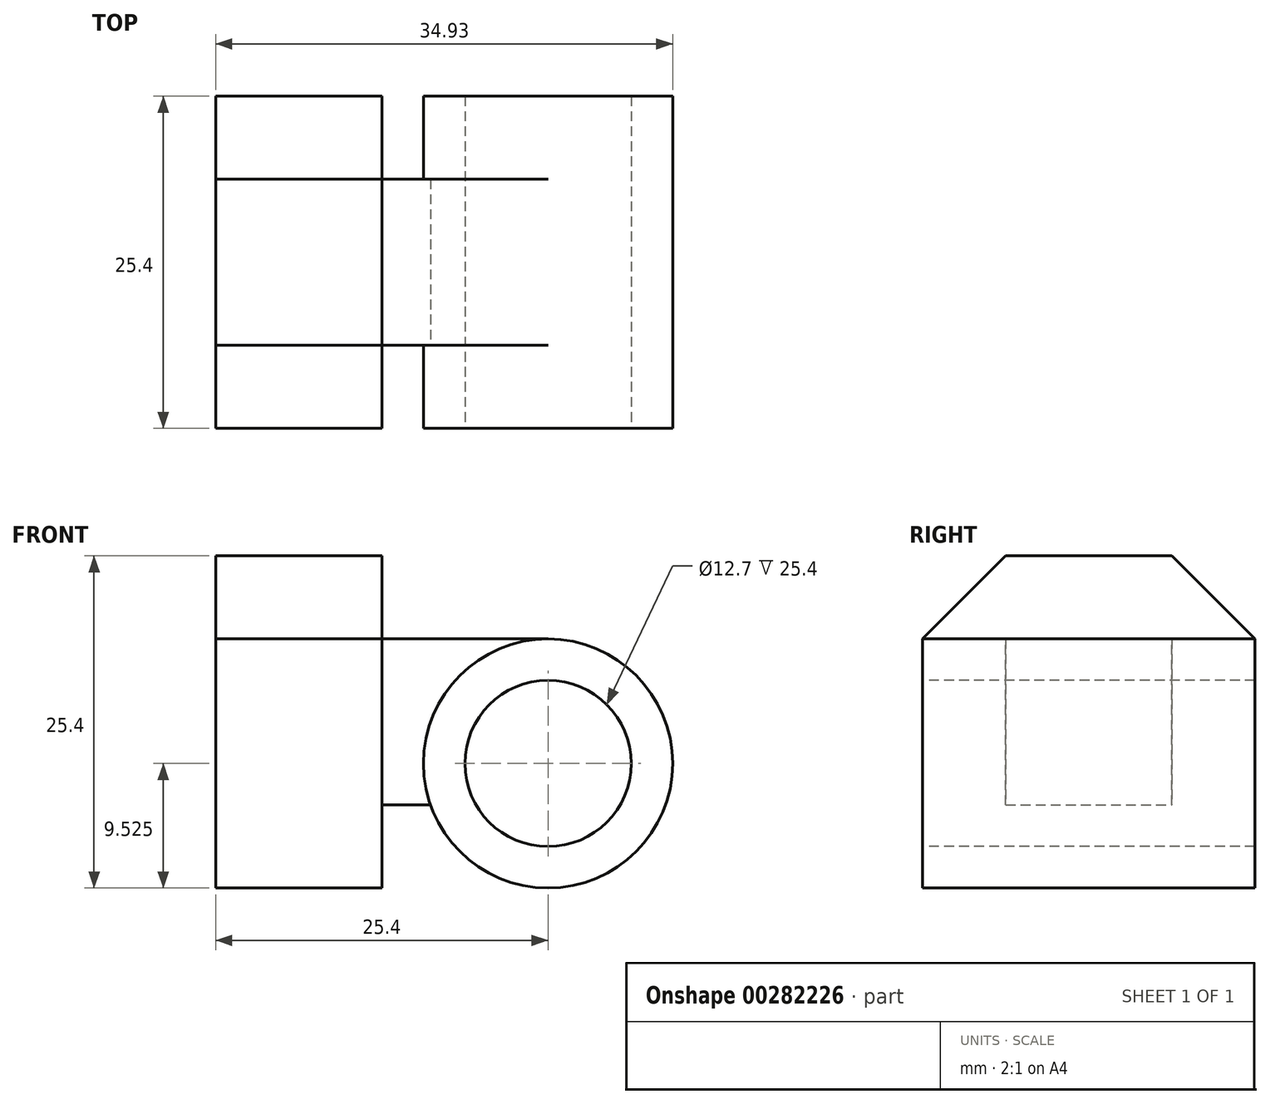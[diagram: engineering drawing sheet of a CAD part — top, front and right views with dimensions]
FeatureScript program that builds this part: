
annotation { "Feature Type Name" : "Feature", "Feature Type Description" : "" }
export const myFeature = defineFeature(function(context is Context, id is Id, definition is map)
    precondition{}
    {
        {
            var Q0;
            Q0=qCreatedBy(makeId("Front.planeOp"),FACE);
            var sketch = newSketch(context, id + "F0", { "sketchPlane" : qUnion([Q0])});
            skLineSegment(sketch, "E0.bottom", {"start": v(0, 0) * mm, "end": v(12.7, 0) * mm});
            skLineSegment(sketch, "E0.top", {"start": v(0, 25.4) * mm, "end": v(12.7, 25.4) * mm});
            skLineSegment(sketch, "E0.left", {"start": v(0, 0) * mm, "end": v(0, 25.4) * mm});
            skLineSegment(sketch, "E0.right", {"start": v(12.7, 0) * mm, "end": v(12.7, 25.4) * mm});
            skSolve(sketch);
        }
        {
            var Q0;
            Q0=makeQuery(id+"F0.imprint","IMPRINT",FACE,{"disambiguationData":[TD([[makeQuery(id+"F0.imprint","IMPRINT",EDGE,{"derivedFrom":sQuery(id+"F0.wireOp",EDGE,"E0.bottom")}),1.0]])]});
            extrude(context, id + "F1", {"entities" : qUnion([Q0]), "endBound" : BoundingType.SYMMETRIC, "depth" : 25.4 * mm});
        }
        {
            var Q0;
            Q0=makeQuery(id+"F1.opExtrude","SWEPT_FACE",FACE,{"disambiguationData":[OSD([sQuery(id+"F0.wireOp",EDGE,"E0.right")])]});
            var sketch = newSketch(context, id + "F2", { "sketchPlane" : qUnion([Q0])});
            skLineSegment(sketch, "E1", {"start": v(-12.7, 19.05) * mm, "end": v(-12.7, 25.4) * mm});
            skLineSegment(sketch, "E2", {"start": v(-12.7, 25.4) * mm, "end": v(-6.35, 25.4) * mm});
            skLineSegment(sketch, "E3", {"start": v(-6.35, 25.4) * mm, "end": v(-12.7, 19.05) * mm});
            skLineSegment(sketch, "E4", {"start": v(6.35, 25.4) * mm, "end": v(12.7, 19.05) * mm});
            skLineSegment(sketch, "E5", {"start": v(12.7, 19.05) * mm, "end": v(12.7, 25.4) * mm});
            skLineSegment(sketch, "E6", {"start": v(12.7, 25.4) * mm, "end": v(6.35, 25.4) * mm});
            skSolve(sketch);
        }
        {
            var Q0;
            Q0=makeQuery(id+"F2.imprint","IMPRINT",FACE,{"disambiguationData":[TD([[makeQuery(id+"F2.imprint","IMPRINT",EDGE,{"derivedFrom":sQuery(id+"F2.wireOp",EDGE,"E1")}),-1.0]])]});
            var Q1;
            Q1=makeQuery(id+"F2.imprint","IMPRINT",FACE,{"disambiguationData":[TD([[makeQuery(id+"F2.imprint","IMPRINT",EDGE,{"derivedFrom":sQuery(id+"F2.wireOp",EDGE,"E4")}),1.0]])]});
            extrude(context, id + "F3", {"entities" : qUnion([Q0, Q1]), "operationType" : NewBodyOperationType.REMOVE, "oppositeDirection" : true, "depth" : 12.7 * mm});
        }
        {
            var Q0;
            Q0=makeQuery(id+"F1.opExtrude","SWEPT_FACE",FACE,{"disambiguationData":[OSD([sQuery(id+"F0.wireOp",EDGE,"E0.right")])]});
            var sketch = newSketch(context, id + "F4", { "sketchPlane" : qUnion([Q0])});
            skLineSegment(sketch, "E7.bottom", {"start": v(-6.35, 19.05) * mm, "end": v(6.35, 19.05) * mm});
            skLineSegment(sketch, "E7.top", {"start": v(-6.35, 6.35) * mm, "end": v(6.35, 6.35) * mm});
            skLineSegment(sketch, "E7.left", {"start": v(-6.35, 19.05) * mm, "end": v(-6.35, 6.35) * mm});
            skLineSegment(sketch, "E7.right", {"start": v(6.35, 19.05) * mm, "end": v(6.35, 6.35) * mm});
            skSolve(sketch);
        }
        {
            var Q0;
            Q0=makeQuery(id+"F4.imprint","IMPRINT",FACE,{"disambiguationData":[TD([[makeQuery(id+"F4.imprint","IMPRINT",EDGE,{"derivedFrom":sQuery(id+"F4.wireOp",EDGE,"E7.bottom")}),-1.0]])]});
            extrude(context, id + "F5", {"entities" : qUnion([Q0]), "operationType" : NewBodyOperationType.ADD, "depth" : 12.7 * mm});
        }
        {
            var Q0;
            Q0=qCreatedBy(makeId("Front.planeOp"),FACE);
            var sketch = newSketch(context, id + "F6", { "sketchPlane" : qUnion([Q0])});
            skCircle(sketch, "E8", {"center": v(25.4, 9.52) * mm, "radius": 9.53 * mm});
            skSolve(sketch);
        }
        {
            var Q0;
            Q0=makeQuery(id+"F6.imprint","IMPRINT",FACE,{"disambiguationData":[TD([[makeQuery(id+"F6.imprint","IMPRINT",EDGE,{"derivedFrom":sQuery(id+"F6.wireOp",EDGE,"E8")}),1.0]])]});
            extrude(context, id + "F7", {"entities" : qUnion([Q0]), "operationType" : NewBodyOperationType.ADD, "endBound" : BoundingType.SYMMETRIC, "oppositeDirection" : true, "depth" : 25.4 * mm});
        }
        {
            var Q0;
            Q0=makeQuery(id+"F7.opExtrude","CAP_FACE",FACE,{"disambiguationData":[OSD([sQuery(id+"F6.wireOp",EDGE,"E8")])],"isStart":true});
            var sketch = newSketch(context, id + "F8", { "sketchPlane" : qUnion([Q0])});
            skCircle(sketch, "E9", {"center": v(25.4, 9.52) * mm, "radius": 6.35 * mm});
            skSolve(sketch);
        }
        {
            var Q0;
            Q0 = qSketchRegion(id + "F8", true);
            extrude(context, id + "F9", {"entities" : qUnion([Q0]), "operationType" : NewBodyOperationType.REMOVE, "oppositeDirection" : true, "depth" : 25.4 * mm});
        }
    });
